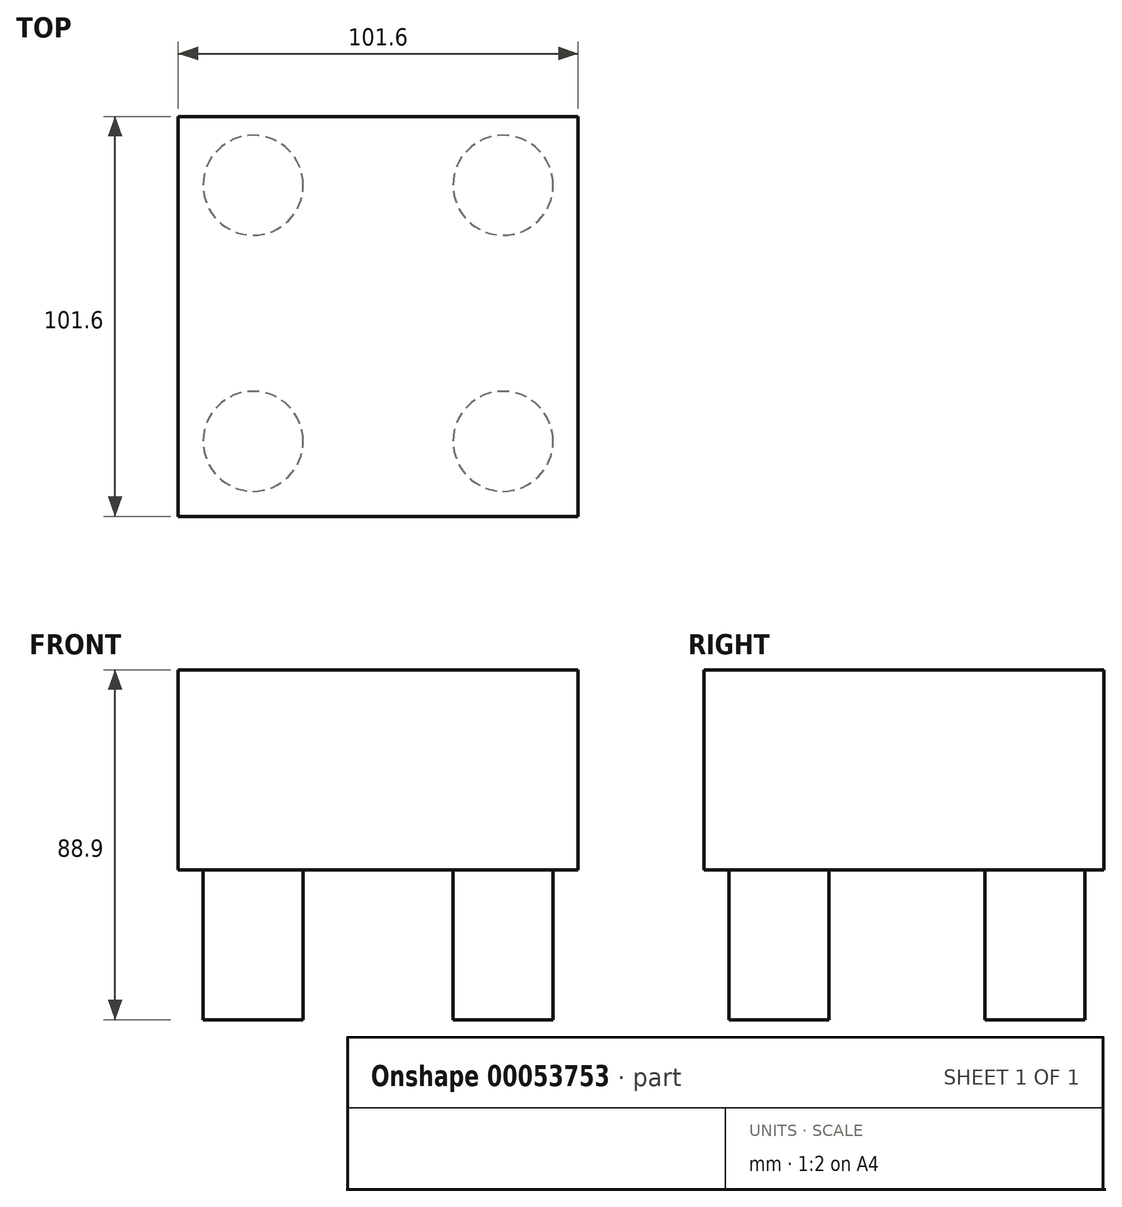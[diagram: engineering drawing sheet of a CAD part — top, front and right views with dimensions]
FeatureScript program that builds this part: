
annotation { "Feature Type Name" : "Feature", "Feature Type Description" : "" }
export const myFeature = defineFeature(function(context is Context, id is Id, definition is map)
    precondition{}
    {
        {
            var Q0;
            Q0=qCreatedBy(makeId("Top.planeOp"),FACE);
            var sketch = newSketch(context, id + "F0", { "sketchPlane" : qUnion([Q0])});
            skLineSegment(sketch, "E0.bottom", {"start": v(-50.8, 50.03) * mm, "end": v(50.8, 50.03) * mm});
            skLineSegment(sketch, "E0.top", {"start": v(-50.8, -51.57) * mm, "end": v(50.8, -51.57) * mm});
            skLineSegment(sketch, "E0.left", {"start": v(-50.8, 50.03) * mm, "end": v(-50.8, -51.57) * mm});
            skLineSegment(sketch, "E0.right", {"start": v(50.8, 50.03) * mm, "end": v(50.8, -51.57) * mm});
            skSolve(sketch);
        }
        {
            var Q0;
            Q0=makeQuery(id+"F0.imprint","IMPRINT",FACE,{"disambiguationData":[TD([[makeQuery(id+"F0.imprint","IMPRINT",EDGE,{"derivedFrom":sQuery(id+"F0.wireOp",EDGE,"E0.bottom")}),-1.0]])]});
            extrude(context, id + "F1", {"entities" : qUnion([Q0]), "depth" : 50.8 * mm});
        }
        {
            var Q0;
            Q0=makeQuery(id+"F0.imprint","IMPRINT",FACE,{"disambiguationData":[TD([[makeQuery(id+"F0.imprint","IMPRINT",EDGE,{"derivedFrom":sQuery(id+"F0.wireOp",EDGE,"E0.bottom")}),-1.0]])]});
            var sketch = newSketch(context, id + "F2", { "sketchPlane" : qUnion([Q0])});
            skCircle(sketch, "E1", {"center": v(31.75, -32.52) * mm, "radius": 12.7 * mm});
            skCircle(sketch, "E2.MirrorC", {"center": v(-31.75, -32.52) * mm, "radius": 12.7 * mm});
            skCircle(sketch, "E3.MirrorC", {"center": v(31.75, 32.52) * mm, "radius": 12.7 * mm});
            skCircle(sketch, "E4.MirrorC", {"center": v(-31.75, 32.52) * mm, "radius": 12.7 * mm});
            skSolve(sketch);
        }
        {
            var Q0;
            Q0 = qSketchRegion(id + "F2", true);
            extrude(context, id + "F3", {"entities" : qUnion([Q0]), "operationType" : NewBodyOperationType.ADD, "oppositeDirection" : true, "depth" : 38.1 * mm});
        }
    });
